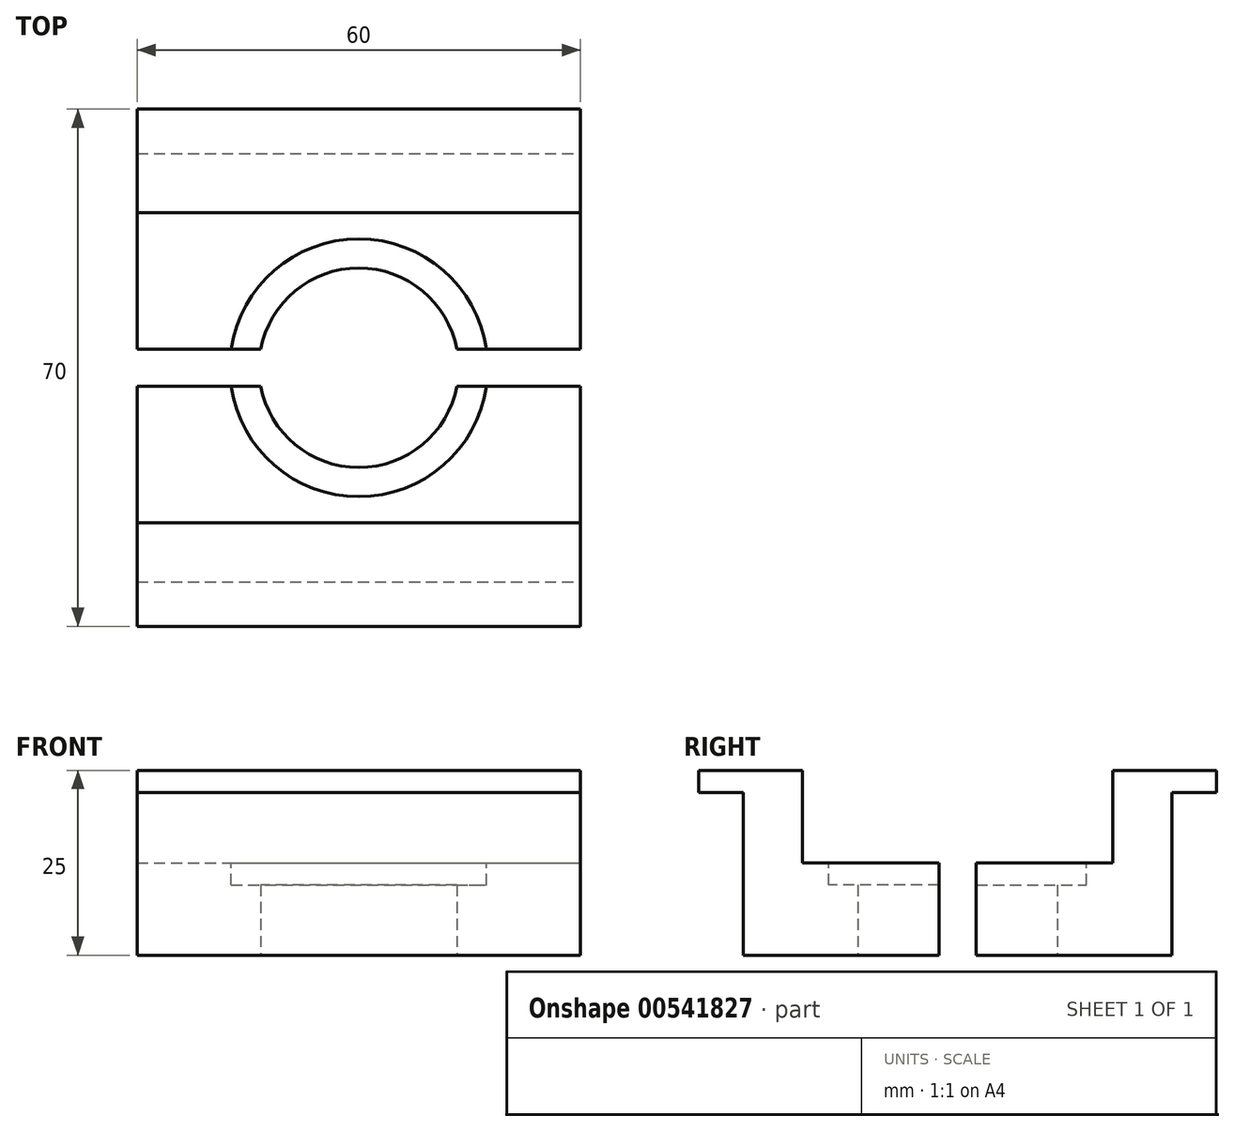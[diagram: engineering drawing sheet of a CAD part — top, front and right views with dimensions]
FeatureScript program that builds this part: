
annotation { "Feature Type Name" : "Feature", "Feature Type Description" : "" }
export const myFeature = defineFeature(function(context is Context, id is Id, definition is map)
    precondition{}
    {
        {
            var Q0;
            Q0=qCreatedBy(makeId("Top.planeOp"),FACE);
            var sketch = newSketch(context, id + "F0", { "sketchPlane" : qUnion([Q0])});
            skLineSegment(sketch, "E0.bottom", {"start": v(-30, 35) * mm, "end": v(30, 35) * mm});
            skLineSegment(sketch, "E0.top", {"start": v(-30, -35) * mm, "end": v(30, -35) * mm});
            skLineSegment(sketch, "E0.left", {"start": v(-30, 35) * mm, "end": v(-30, -35) * mm});
            skLineSegment(sketch, "E0.right", {"start": v(30, 35) * mm, "end": v(30, -35) * mm});
            skCircle(sketch, "E1", {"center": v(0, 0) * mm, "radius": 13.5 * mm});
            skSolve(sketch);
        }
        {
            var Q0;
            Q0=makeQuery(id+"F0.imprint","IMPRINT",FACE,{"disambiguationData":[TD([[makeQuery(id+"F0.imprint","IMPRINT",EDGE,{"derivedFrom":sQuery(id+"F0.wireOp",EDGE,"E0.bottom")}),-1.0]])]});
            extrude(context, id + "F1", {"entities" : qUnion([Q0]), "depth" : 25 * mm, "offsetDistance" : 25.4 * mm});
        }
        {
            var Q0;
            Q0=makeQuery(id+"F1.opExtrude","SWEPT_FACE",FACE,{"disambiguationData":[OSD([sQuery(id+"F0.wireOp",EDGE,"E0.right")])]});
            var sketch = newSketch(context, id + "F2", { "sketchPlane" : qUnion([Q0])});
            skLineSegment(sketch, "E2.bottom", {"start": v(-35, 0) * mm, "end": v(-29, 0) * mm});
            skLineSegment(sketch, "E2.top", {"start": v(-35, 22) * mm, "end": v(-29, 22) * mm});
            skLineSegment(sketch, "E2.left", {"start": v(-35, 0) * mm, "end": v(-35, 22) * mm});
            skLineSegment(sketch, "E2.right", {"start": v(-29, 0) * mm, "end": v(-29, 22) * mm});
            skLineSegment(sketch, "E3.bottom", {"start": v(35, 0) * mm, "end": v(29, 0) * mm});
            skLineSegment(sketch, "E3.top", {"start": v(35, 22) * mm, "end": v(29, 22) * mm});
            skLineSegment(sketch, "E3.left", {"start": v(35, 0) * mm, "end": v(35, 22) * mm});
            skLineSegment(sketch, "E3.right", {"start": v(29, 0) * mm, "end": v(29, 22) * mm});
            skSolve(sketch);
        }
        {
            var Q0;
            Q0=makeQuery(id+"F2.imprint","IMPRINT",FACE,{"disambiguationData":[TD([[makeQuery(id+"F2.imprint","IMPRINT",EDGE,{"derivedFrom":sQuery(id+"F2.wireOp",EDGE,"E2.bottom")}),-1.0]])]});
            extrude(context, id + "F3", {"entities" : qUnion([Q0]), "operationType" : NewBodyOperationType.REMOVE, "endBound" : BoundingType.THROUGH_ALL, "oppositeDirection" : true, "depth" : 25.4 * mm, "offsetDistance" : 25.4 * mm});
        }
        {
            var Q0;
            Q0 = qSketchRegion(id + "F2", true);
            extrude(context, id + "F4", {"entities" : qUnion([Q0]), "operationType" : NewBodyOperationType.REMOVE, "endBound" : BoundingType.THROUGH_ALL, "oppositeDirection" : true, "depth" : 25.4 * mm, "offsetDistance" : 25.4 * mm});
        }
        {
            var Q0;
            Q0=makeQuery(id+"F1.opExtrude","SWEPT_FACE",FACE,{"disambiguationData":[OSD([sQuery(id+"F0.wireOp",EDGE,"E0.right")])]});
            var sketch = newSketch(context, id + "F5", { "sketchPlane" : qUnion([Q0])});
            skLineSegment(sketch, "E4.bottom", {"start": v(-21, 25) * mm, "end": v(21, 25) * mm});
            skLineSegment(sketch, "E4.top", {"start": v(-21, 12.5) * mm, "end": v(21, 12.5) * mm});
            skLineSegment(sketch, "E4.left", {"start": v(-21, 25) * mm, "end": v(-21, 12.5) * mm});
            skLineSegment(sketch, "E4.right", {"start": v(21, 25) * mm, "end": v(21, 12.5) * mm});
            skSolve(sketch);
        }
        {
            var Q0;
            Q0=makeQuery(id+"F5.imprint","IMPRINT",FACE,{"disambiguationData":[TD([[makeQuery(id+"F5.imprint","IMPRINT",EDGE,{"derivedFrom":sQuery(id+"F5.wireOp",EDGE,"E4.bottom")}),1.0]])]});
            extrude(context, id + "F6", {"entities" : qUnion([Q0]), "operationType" : NewBodyOperationType.REMOVE, "endBound" : BoundingType.THROUGH_ALL, "oppositeDirection" : true, "depth" : 25.4 * mm, "offsetDistance" : 25.4 * mm});
        }
        {
            var Q0;
            Q0=makeQuery(id+"F6.boolean.opBoolean","COPY",FACE,{"derivedFrom":makeQuery(id+"F6.opExtrude","SWEPT_FACE",FACE,{"disambiguationData":[OSD([sQuery(id+"F5.wireOp",EDGE,"E4.top")])]})});
            var sketch = newSketch(context, id + "F7", { "sketchPlane" : qUnion([Q0])});
            skCircle(sketch, "E5", {"center": v(0, 0) * mm, "radius": 17.45 * mm});
            skSolve(sketch);
        }
        {
            var Q0;
            Q0=makeQuery(id+"F7.imprint","IMPRINT",FACE,{"disambiguationData":[TD([[makeQuery(id+"F7.imprint","IMPRINT",EDGE,{"derivedFrom":sQuery(id+"F7.wireOp",EDGE,"E5")}),1.0]])]});
            extrude(context, id + "F8", {"entities" : qUnion([Q0]), "operationType" : NewBodyOperationType.REMOVE, "oppositeDirection" : true, "depth" : 3 * mm, "offsetDistance" : 25.4 * mm});
        }
        {
            var Q0;
            Q0=makeQuery(id+"F1.opExtrude","SWEPT_FACE",FACE,{"disambiguationData":[OSD([sQuery(id+"F0.wireOp",EDGE,"E0.right")])]});
            var sketch = newSketch(context, id + "F9", { "sketchPlane" : qUnion([Q0])});
            skLineSegment(sketch, "E6.bottom", {"start": v(-2.5, 12.5) * mm, "end": v(2.5, 12.5) * mm});
            skLineSegment(sketch, "E6.top", {"start": v(-2.5, 0) * mm, "end": v(2.5, 0) * mm});
            skLineSegment(sketch, "E6.left", {"start": v(-2.5, 12.5) * mm, "end": v(-2.5, 0) * mm});
            skLineSegment(sketch, "E6.right", {"start": v(2.5, 12.5) * mm, "end": v(2.5, 0) * mm});
            skSolve(sketch);
        }
        {
            var Q0;
            Q0 = qSketchRegion(id + "F9", true);
            extrude(context, id + "F10", {"entities" : qUnion([Q0]), "operationType" : NewBodyOperationType.REMOVE, "endBound" : BoundingType.THROUGH_ALL, "oppositeDirection" : true, "depth" : 25.4 * mm, "offsetDistance" : 25.4 * mm});
        }
    });
